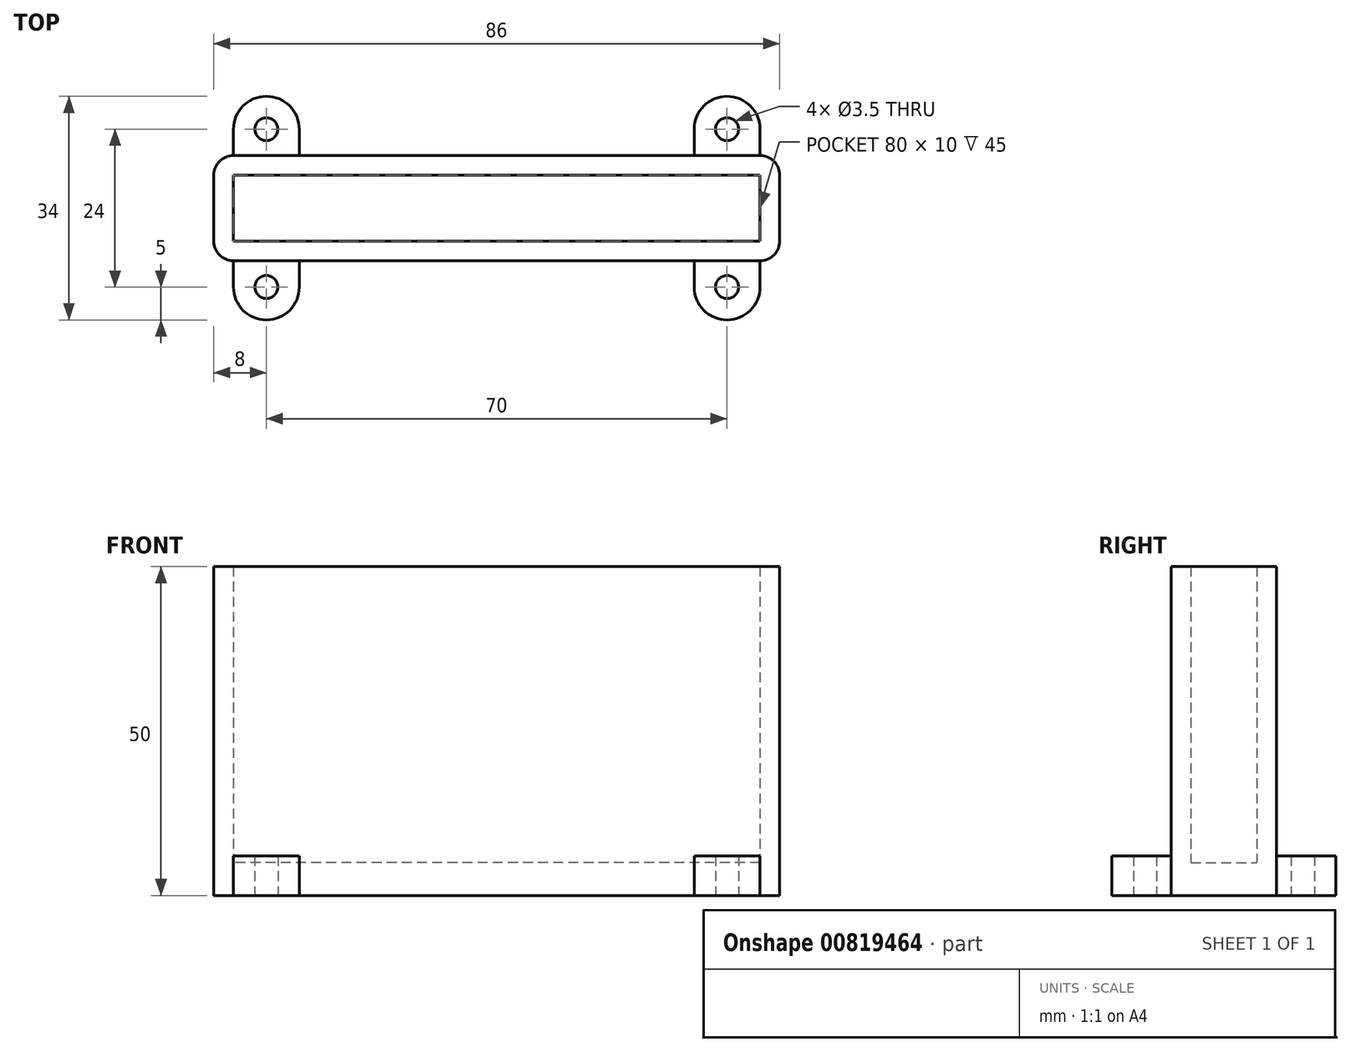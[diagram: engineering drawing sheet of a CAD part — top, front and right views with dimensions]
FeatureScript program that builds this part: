
annotation { "Feature Type Name" : "Feature", "Feature Type Description" : "" }
export const myFeature = defineFeature(function(context is Context, id is Id, definition is map)
    precondition{}
    {
        {
            var Q0;
            Q0=qCreatedBy(makeId("Top.planeOp"),FACE);
            var sketch = newSketch(context, id + "F0", { "sketchPlane" : qUnion([Q0])});
            skLineSegment(sketch, "E0.bottom", {"start": v(40, -5) * mm, "end": v(-40, -5) * mm});
            skLineSegment(sketch, "E0.top", {"start": v(40, 5) * mm, "end": v(-40, 5) * mm});
            skLineSegment(sketch, "E0.left", {"start": v(40, -5) * mm, "end": v(40, 5) * mm});
            skLineSegment(sketch, "E0.right", {"start": v(-40, -5) * mm, "end": v(-40, 5) * mm});
            skPoint(sketch, "E0.middle", {"position": v(0, 0) * mm});
            skLineSegment(sketch, "E1.0", {"start": v(40, 8) * mm, "end": v(-40, 8) * mm});
            skLineSegment(sketch, "E1.1", {"start": v(43, -5) * mm, "end": v(43, 5) * mm});
            skLineSegment(sketch, "E1.2", {"start": v(40, -8) * mm, "end": v(-40, -8) * mm});
            skLineSegment(sketch, "E1.3", {"start": v(-43, -5) * mm, "end": v(-43, 5) * mm});
            skPoint(sketch, "E2.visualSharp", {"position": v(-43, 8) * mm});
            skArc(sketch, "E2.filletArc", {"start": v(-40, 8) * mm, "mid": v(-42.12, 7.12) * mm, "end": v(-43, 5) * mm});
            skPoint(sketch, "E3.visualSharp", {"position": v(-43, -8) * mm});
            skArc(sketch, "E3.filletArc", {"start": v(-43, -5) * mm, "mid": v(-42.12, -7.12) * mm, "end": v(-40, -8) * mm});
            skPoint(sketch, "E4.visualSharp", {"position": v(43, 8) * mm});
            skArc(sketch, "E4.filletArc", {"start": v(43, 5) * mm, "mid": v(42.12, 7.12) * mm, "end": v(40, 8) * mm});
            skPoint(sketch, "E5.visualSharp", {"position": v(43, -8) * mm});
            skArc(sketch, "E5.filletArc", {"start": v(40, -8) * mm, "mid": v(42.12, -7.12) * mm, "end": v(43, -5) * mm});
            skLineSegment(sketch, "E6", {"start": v(40, -8) * mm, "end": v(40, -12) * mm});
            skLineSegment(sketch, "E7", {"start": v(-40, 8) * mm, "end": v(-40, 12) * mm});
            skLineSegment(sketch, "E8", {"start": v(-30, 12) * mm, "end": v(-40, 12) * mm});
            skLineSegment(sketch, "E9", {"start": v(-30, 12) * mm, "end": v(-30, 8) * mm});
            skLineSegment(sketch, "E10", {"start": v(40, 8) * mm, "end": v(40, 12) * mm});
            skLineSegment(sketch, "E11", {"start": v(40, 12) * mm, "end": v(30, 12) * mm});
            skLineSegment(sketch, "E12", {"start": v(30, 12) * mm, "end": v(30, 8) * mm});
            skArc(sketch, "E13", {"start": v(-30, 12) * mm, "mid": v(-35, 17) * mm, "end": v(-40, 12) * mm});
            skArc(sketch, "E14", {"start": v(40, 12) * mm, "mid": v(35, 17) * mm, "end": v(30, 12) * mm});
            skCircle(sketch, "E15", {"center": v(-35, 12) * mm, "radius": 1.75 * mm});
            skCircle(sketch, "E16", {"center": v(35, 12) * mm, "radius": 1.75 * mm});
            skLineSegment(sketch, "E17", {"start": v(40, -12) * mm, "end": v(30, -12) * mm});
            skLineSegment(sketch, "E18", {"start": v(30, -12) * mm, "end": v(30, -8) * mm});
            skLineSegment(sketch, "E19", {"start": v(-40, -8) * mm, "end": v(-40, -12) * mm});
            skLineSegment(sketch, "E20", {"start": v(-30, -12) * mm, "end": v(-40, -12) * mm});
            skLineSegment(sketch, "E21", {"start": v(-30, -12) * mm, "end": v(-30, -8) * mm});
            skArc(sketch, "E22", {"start": v(30, -12) * mm, "mid": v(35, -17) * mm, "end": v(40, -12) * mm});
            skArc(sketch, "E23", {"start": v(-40, -12) * mm, "mid": v(-35, -17) * mm, "end": v(-30, -12) * mm});
            skCircle(sketch, "E24", {"center": v(-35, -12) * mm, "radius": 1.75 * mm});
            skCircle(sketch, "E25", {"center": v(35, -12) * mm, "radius": 1.75 * mm});
            skSolve(sketch);
        }
        {
            var Q0;
            Q0=makeQuery(id+"F0.imprint","IMPRINT",FACE,{"disambiguationData":[TD([[makeQuery(id+"F0.imprint","IMPRINT",EDGE,{"derivedFrom":sQuery(id+"F0.wireOp",EDGE,"E0.bottom")}),1.0]])]});
            extrude(context, id + "F1", {"entities" : qUnion([Q0]), "depth" : 50 * mm, "offsetDistance" : 25 * mm});
        }
        {
            var Q0;
            Q0=qCreatedBy(makeId("Top.planeOp"),FACE);
            var sketch = newSketch(context, id + "F2", { "sketchPlane" : qUnion([Q0])});
            skLineSegment(sketch, "E26.bottom", {"start": v(40, -5) * mm, "end": v(-40, -5) * mm});
            skLineSegment(sketch, "E26.top", {"start": v(40, 5) * mm, "end": v(-40, 5) * mm});
            skLineSegment(sketch, "E26.left", {"start": v(40, -5) * mm, "end": v(40, 5) * mm});
            skLineSegment(sketch, "E26.right", {"start": v(-40, -5) * mm, "end": v(-40, 5) * mm});
            skPoint(sketch, "E26.middle", {"position": v(0, 0) * mm});
            skSolve(sketch);
        }
        {
            var Q0;
            Q0=makeQuery(id+"F2.imprint","IMPRINT",FACE,{"disambiguationData":[TD([[makeQuery(id+"F2.imprint","IMPRINT",EDGE,{"derivedFrom":sQuery(id+"F2.wireOp",EDGE,"E26.bottom")}),-1.0]])]});
            extrude(context, id + "F3", {"entities" : qUnion([Q0]), "operationType" : NewBodyOperationType.ADD, "depth" : 5 * mm, "offsetDistance" : 25 * mm});
        }
        {
            var Q0;
            Q0=qSketchRegion(id+"F0",true);
            extrude(context, id + "F4", {"entities" : qUnion([Q0]), "operationType" : NewBodyOperationType.ADD, "depth" : 6 * mm, "offsetDistance" : 25 * mm});
        }
    });
